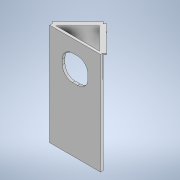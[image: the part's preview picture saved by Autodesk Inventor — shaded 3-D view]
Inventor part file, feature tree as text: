
AUTODESK INVENTOR PART (.ipt)
format: ipt  version: 2020 (Build 240168000, 168)  size: 165,888 bytes
history: native  units: mm
features: extrude x4, sketch x4
ambient origin geometry x8: Origin, YZ Plane, XZ Plane, XY Plane, X Axis, Y Axis, Z Axis, Center Point
bodies: Solid1 (feature_tree)
feature tree (8):
  extrude  "Extrusion1"  Depth=200.0mm
  extrude  "Extrusion2"  TaperAngle=45.0deg  [1 undecoded]
  extrude  "Extrusion6"  Depth=5.0mm
  extrude  "Extrusion9"  Depth=50.0mm
  sketch  "Sketch1"  dims[d0=100.0mm d1=200.0mm]
  sketch  "Sketch2"  dims[d2=5.0mm d3=0.0mm d4=45.0deg]
  sketch  "Sketch6"  dims[d5=5.0mm d6=5.0mm]
  sketch  "Sketch10"  dims[d7=45.0mm d8=0.0mm d21=50.0mm d22=50.0mm d23=20.0mm d24=5.0mm d25=0.0mm d33=5.0mm d34=5.0mm d36=3.0mm d37=0.0mm]
note: 1 required parameter value undecoded (feature->parameter linkage not recoverable at this tier; creation-order binding heuristic only, values carry confidence <= 0.55)
